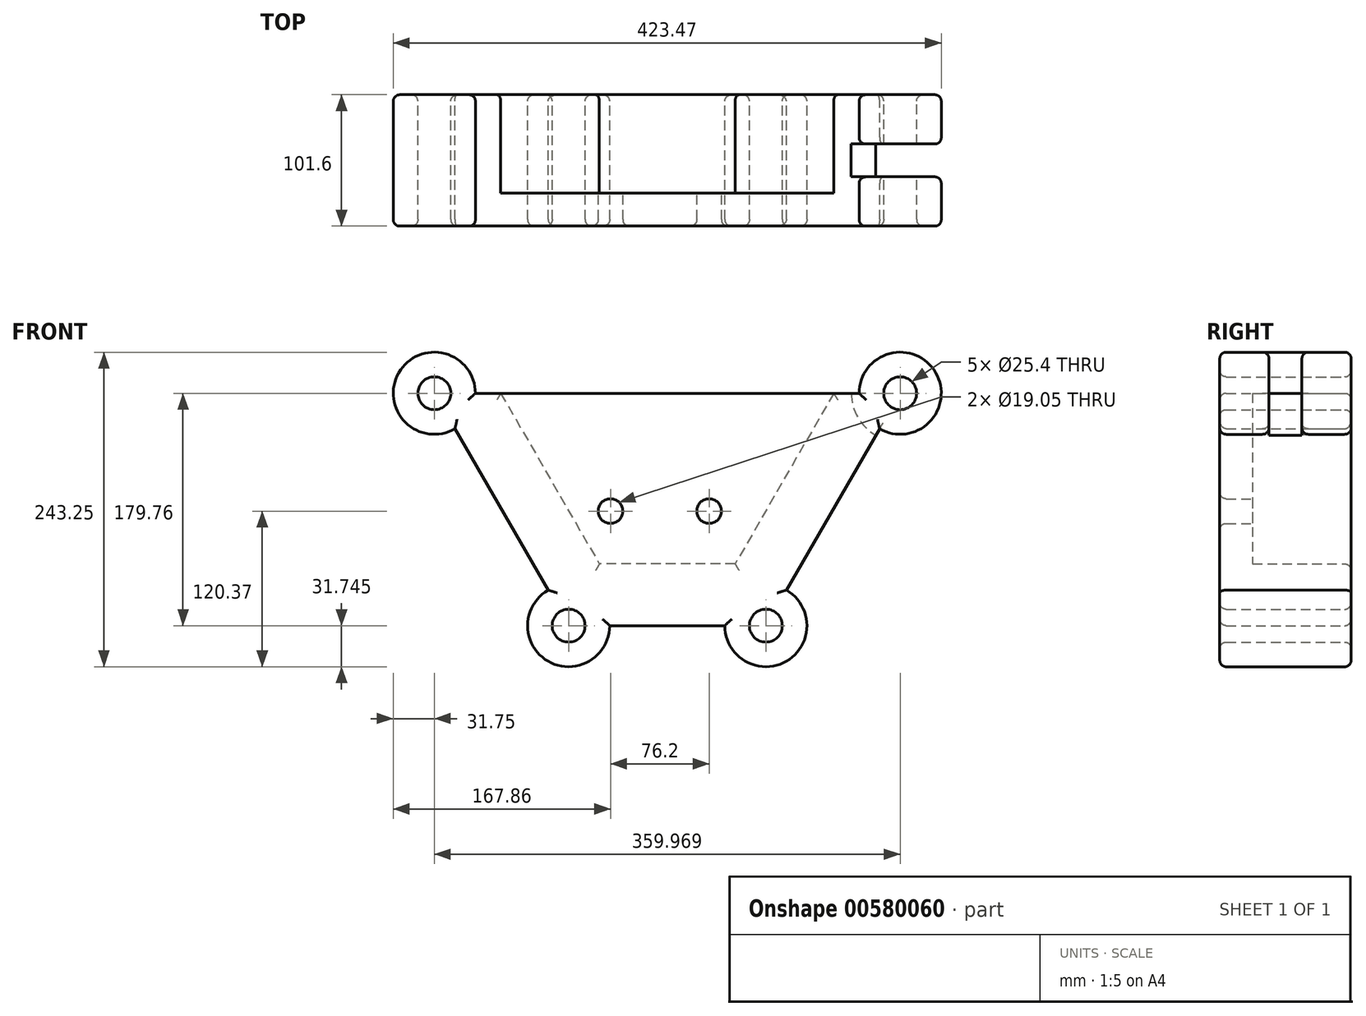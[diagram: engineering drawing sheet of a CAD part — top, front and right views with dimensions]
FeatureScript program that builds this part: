
annotation { "Feature Type Name" : "Feature", "Feature Type Description" : "" }
export const myFeature = defineFeature(function(context is Context, id is Id, definition is map)
    precondition{}
    {
        {
            var Q0;
            Q0=qCreatedBy(makeId("Front.planeOp"),FACE);
            var sketch = newSketch(context, id + "F0", { "sketchPlane" : qUnion([Q0])});
            skArc(sketch, "E0", {"start": v(-142.46, 91.13) * mm, "mid": v(-201.7, 107) * mm, "end": v(-158.33, 63.64) * mm});
            skCircle(sketch, "E1", {"center": v(-174.2, 91.13) * mm, "radius": 12.7 * mm});
            skArc(sketch, "E2", {"start": v(169.88, 63.64) * mm, "mid": v(213.26, 107) * mm, "end": v(154, 91.13) * mm});
            skCircle(sketch, "E3", {"center": v(185.76, 91.13) * mm, "radius": 12.7 * mm});
            skArc(sketch, "E4", {"start": v(50.22, -88.62) * mm, "mid": v(97.85, -116.12) * mm, "end": v(97.85, -61.13) * mm});
            skCircle(sketch, "E5", {"center": v(81.97, -88.62) * mm, "radius": 12.7 * mm});
            skArc(sketch, "E6", {"start": v(-86.3, -61.13) * mm, "mid": v(-86.3, -116.12) * mm, "end": v(-38.68, -88.62) * mm});
            skCircle(sketch, "E7", {"center": v(-70.43, -88.62) * mm, "radius": 12.7 * mm});
            skLineSegment(sketch, "E8.trimOffspring", {"start": v(-86.3, -61.13) * mm, "end": v(-158.33, 63.64) * mm});
            skLineSegment(sketch, "E9.trimOffspring", {"start": v(-38.68, -88.62) * mm, "end": v(50.22, -88.62) * mm});
            skLineSegment(sketch, "E10.trimOffspring", {"start": v(97.85, -61.13) * mm, "end": v(169.88, 63.64) * mm});
            skLineSegment(sketch, "E11.trimOffspring", {"start": v(-142.46, 91.13) * mm, "end": v(154, 91.13) * mm});
            skSolve(sketch);
        }
        {
            var Q0;
            Q0 = qSketchRegion(id + "F0", true);
            extrude(context, id + "F1", {"entities" : qUnion([Q0]), "endBound" : BoundingType.SYMMETRIC, "depth" : -101.6 * mm, "offsetDistance" : 25.4 * mm});
        }
        {
            var Q0;
            Q0=makeQuery(id+"F1.opExtrude","CAP_FACE",FACE,{"disambiguationData":[OSD([sQuery(id+"F0.wireOp",EDGE,"E0"),sQuery(id+"F0.wireOp",EDGE,"E1"),sQuery(id+"F0.wireOp",EDGE,"E2"),sQuery(id+"F0.wireOp",EDGE,"E3"),sQuery(id+"F0.wireOp",EDGE,"E4"),sQuery(id+"F0.wireOp",EDGE,"E5"),sQuery(id+"F0.wireOp",EDGE,"E6"),sQuery(id+"F0.wireOp",EDGE,"E7"),sQuery(id+"F0.wireOp",EDGE,"E8.trimOffspring"),sQuery(id+"F0.wireOp",EDGE,"E9.trimOffspring"),sQuery(id+"F0.wireOp",EDGE,"E10.trimOffspring"),sQuery(id+"F0.wireOp",EDGE,"E11.trimOffspring")])],"isStart":true});
            var sketch = newSketch(context, id + "F2", { "sketchPlane" : qUnion([Q0])});
            skLineSegment(sketch, "E12", {"start": v(-134.43, 91.13) * mm, "end": v(-58.23, -40.85) * mm});
            skLineSegment(sketch, "E13", {"start": v(122.88, 91.13) * mm, "end": v(46.68, -40.85) * mm});
            skLineSegment(sketch, "E14", {"start": v(-58.23, -40.85) * mm, "end": v(46.68, -40.85) * mm});
            skSolve(sketch);
        }
        {
            var Q0;
            Q0 = qSketchRegion(id + "F2", true);
            var Q1;
            {var subQ0=sQuery(id+"F2.wireOp",EDGE,"E12");Q1=makeQuery(id+"F2.imprint","IMPRINT",FACE,{"disambiguationData":[TD([[makeQuery(id+"F2.imprint","IMPRINT",EDGE,{"derivedFrom":subQ0}),1.0]])]});}
            extrude(context, id + "F3", {"entities" : qUnion([Q0, Q1]), "operationType" : NewBodyOperationType.REMOVE, "oppositeDirection" : true, "depth" : 76.2 * mm, "offsetDistance" : 25.4 * mm});
        }
        {
            var Q0;
            Q0=qCreatedBy(makeId("Front.planeOp"),FACE);
            var sketch = newSketch(context, id + "F4", { "sketchPlane" : qUnion([Q0])});
            skCircle(sketch, "E15", {"center": v(186.03, 91.58) * mm, "radius": 38.1 * mm});
            skSolve(sketch);
        }
        {
            var Q0;
            Q0 = qSketchRegion(id + "F4", true);
            extrude(context, id + "F5", {"entities" : qUnion([Q0]), "operationType" : NewBodyOperationType.REMOVE, "endBound" : BoundingType.SYMMETRIC, "oppositeDirection" : true, "depth" : 25.4 * mm, "offsetDistance" : 25.4 * mm});
        }
        {
            var Q0;
            Q0=makeQuery(id+"F3.boolean.opBoolean","COPY",FACE,{"derivedFrom":makeQuery(id+"F3.opExtrude","CAP_FACE",FACE,{"disambiguationData":[OSD([sQuery(id+"F0.wireOp",EDGE,"E11.trimOffspring"),sQuery(id+"F2.wireOp",EDGE,"E12"),sQuery(id+"F2.wireOp",EDGE,"E13"),sQuery(id+"F2.wireOp",EDGE,"E14")])],"isStart":false})});
            var sketch = newSketch(context, id + "F6", { "sketchPlane" : qUnion([Q0])});
            skLineSegment(sketch, "E16", {"start": v(0, -24.33) * mm, "end": v(0, 10.34) * mm, "construction": true});
            skLineSegment(sketch, "E17", {"start": v(-38.1, 0) * mm, "end": v(38.1, 0) * mm});
            skCircle(sketch, "E18", {"center": v(38.1, 0) * mm, "radius": 9.53 * mm});
            skCircle(sketch, "E19", {"center": v(-38.1, 0) * mm, "radius": 9.53 * mm});
            skSolve(sketch);
        }
        {
            var Q0;
            Q0 = qSketchRegion(id + "F6", true);
            extrude(context, id + "F7", {"entities" : qUnion([Q0]), "operationType" : NewBodyOperationType.REMOVE, "endBound" : BoundingType.SYMMETRIC, "oppositeDirection" : true, "depth" : 84.84 * mm, "offsetDistance" : 25.4 * mm});
        }
        {
            var Q0;
            Q0=makeQuery(id+"F5.boolean.opBoolean","INTERSECT",EDGE,{"derivedFrom":[makeQuery(id+"F1.opExtrude","SWEPT_FACE",FACE,{"disambiguationData":[OSD([sQuery(id+"F0.wireOp",EDGE,"E2")])]}),makeQuery(id+"F5.opExtrude","CAP_FACE",FACE,{"disambiguationData":[OSD([sQuery(id+"F4.wireOp",EDGE,"E15")])],"isStart":false})]});
            var Q1;
            Q1=makeQuery(id+"F5.boolean.opBoolean","INTERSECT",EDGE,{"derivedFrom":[makeQuery(id+"F1.opExtrude","SWEPT_FACE",FACE,{"disambiguationData":[OSD([sQuery(id+"F0.wireOp",EDGE,"E2")])]}),makeQuery(id+"F5.opExtrude","CAP_FACE",FACE,{"disambiguationData":[OSD([sQuery(id+"F4.wireOp",EDGE,"E15")])],"isStart":true})]});
            fillet(context, id + "F8", {"entities" : qUnion([Q0, Q1]), "radius" : 5.08 * mm, "tangentPropagation" : true, "allowEdgeOverflow" : false});
        }
        {
            var Q0;
            Q0=makeQuery(id+"F1.opExtrude","CAP_FACE",FACE,{"disambiguationData":[OSD([sQuery(id+"F0.wireOp",EDGE,"E0"),sQuery(id+"F0.wireOp",EDGE,"E1"),sQuery(id+"F0.wireOp",EDGE,"E2"),sQuery(id+"F0.wireOp",EDGE,"E3"),sQuery(id+"F0.wireOp",EDGE,"E4"),sQuery(id+"F0.wireOp",EDGE,"E5"),sQuery(id+"F0.wireOp",EDGE,"E6"),sQuery(id+"F0.wireOp",EDGE,"E7"),sQuery(id+"F0.wireOp",EDGE,"E8.trimOffspring"),sQuery(id+"F0.wireOp",EDGE,"E9.trimOffspring"),sQuery(id+"F0.wireOp",EDGE,"E10.trimOffspring"),sQuery(id+"F0.wireOp",EDGE,"E11.trimOffspring")])],"isStart":false});
            fillet(context, id + "F9", {"entities" : qUnion([Q0]), "radius" : 5.08 * mm, "tangentPropagation" : true, "allowEdgeOverflow" : false});
        }
        {
            var Q0;
            Q0=makeQuery(id+"F1.opExtrude","CAP_FACE",FACE,{"disambiguationData":[OSD([sQuery(id+"F0.wireOp",EDGE,"E0"),sQuery(id+"F0.wireOp",EDGE,"E1"),sQuery(id+"F0.wireOp",EDGE,"E2"),sQuery(id+"F0.wireOp",EDGE,"E3"),sQuery(id+"F0.wireOp",EDGE,"E4"),sQuery(id+"F0.wireOp",EDGE,"E5"),sQuery(id+"F0.wireOp",EDGE,"E6"),sQuery(id+"F0.wireOp",EDGE,"E7"),sQuery(id+"F0.wireOp",EDGE,"E8.trimOffspring"),sQuery(id+"F0.wireOp",EDGE,"E9.trimOffspring"),sQuery(id+"F0.wireOp",EDGE,"E10.trimOffspring"),sQuery(id+"F0.wireOp",EDGE,"E11.trimOffspring")])],"isStart":true});
            fillet(context, id + "F10", {"entities" : qUnion([Q0]), "radius" : 5.08 * mm, "tangentPropagation" : true, "allowEdgeOverflow" : false});
        }
    });
